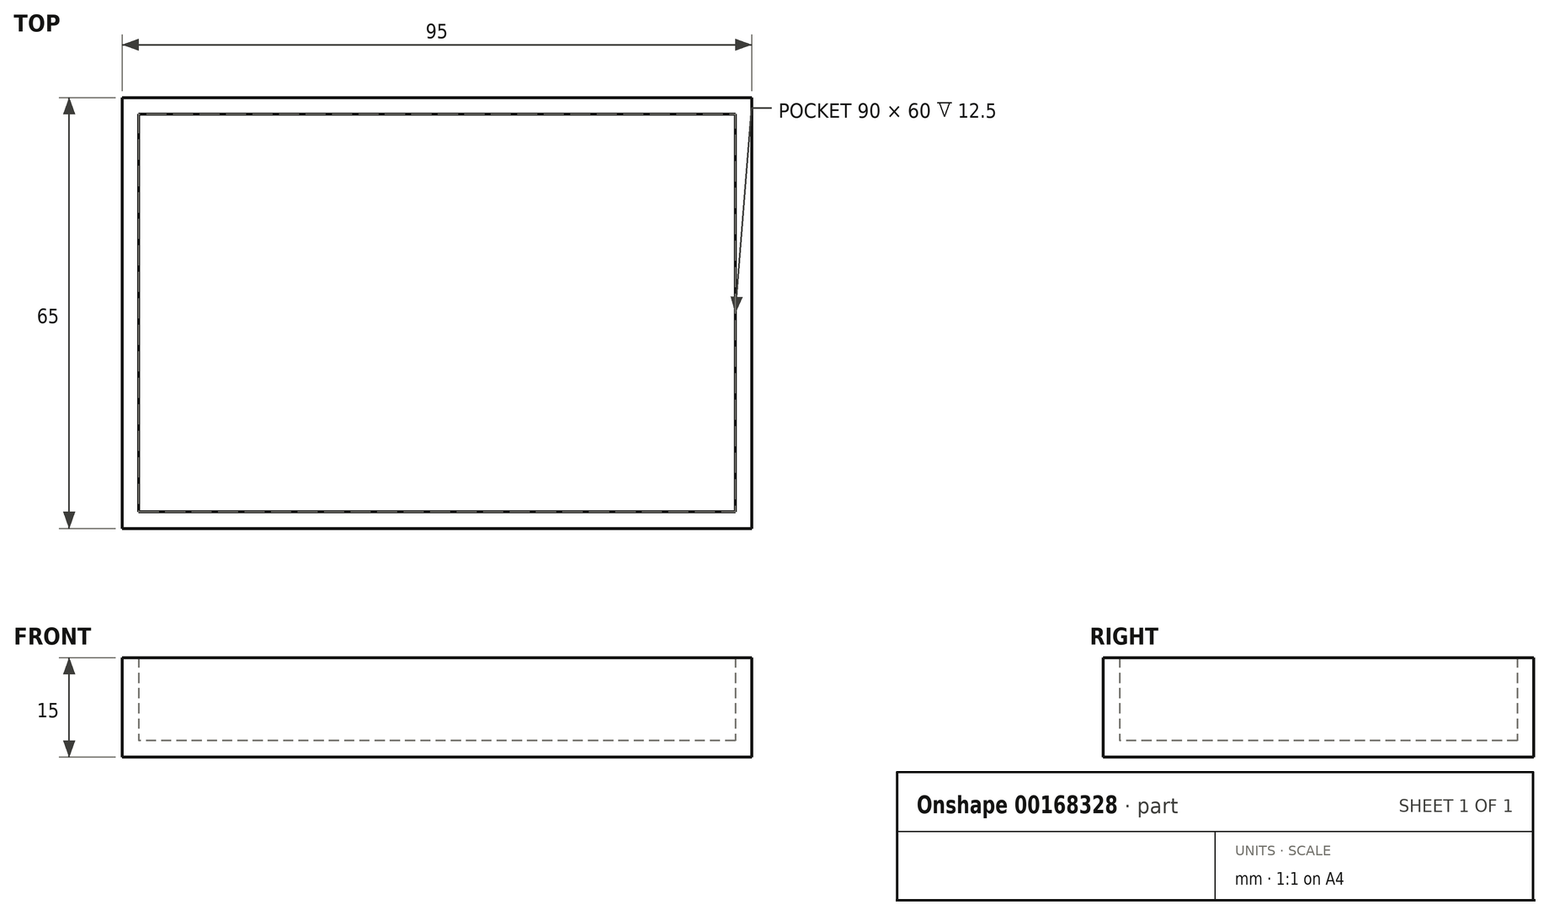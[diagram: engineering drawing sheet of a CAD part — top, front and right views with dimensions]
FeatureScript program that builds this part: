
annotation { "Feature Type Name" : "Feature", "Feature Type Description" : "" }
export const myFeature = defineFeature(function(context is Context, id is Id, definition is map)
    precondition{}
    {
        {
            var Q0;
            Q0=qCreatedBy(makeId("Top.planeOp"),FACE);
            var sketch = newSketch(context, id + "F0", { "sketchPlane" : qUnion([Q0])});
            skLineSegment(sketch, "E0.bottom", {"start": v(47.5, 32.5) * mm, "end": v(-47.5, 32.5) * mm});
            skLineSegment(sketch, "E0.top", {"start": v(47.5, -32.5) * mm, "end": v(-47.5, -32.5) * mm});
            skLineSegment(sketch, "E0.left", {"start": v(47.5, 32.5) * mm, "end": v(47.5, -32.5) * mm});
            skLineSegment(sketch, "E0.right", {"start": v(-47.5, 32.5) * mm, "end": v(-47.5, -32.5) * mm});
            skPoint(sketch, "E0.middle", {"position": v(0, 0) * mm});
            skSolve(sketch);
        }
        {
            var Q0;
            Q0=qSketchRegion(id+"F0",true);
            extrude(context, id + "F1", {"entities" : qUnion([Q0]), "depth" : 15 * mm});
        }
        {
            var Q0;
            Q0=makeQuery(id+"F1.opExtrude","CAP_FACE",FACE,{"disambiguationData":[OSD([sQuery(id+"F0.wireOp",EDGE,"E0.bottom"),sQuery(id+"F0.wireOp",EDGE,"E0.top"),sQuery(id+"F0.wireOp",EDGE,"E0.left"),sQuery(id+"F0.wireOp",EDGE,"E0.right")])],"isStart":false});
            shell(context, id + "F2", {"entities" : qUnion([Q0]), "thickness" : 2.5 * mm});
        }
    });
